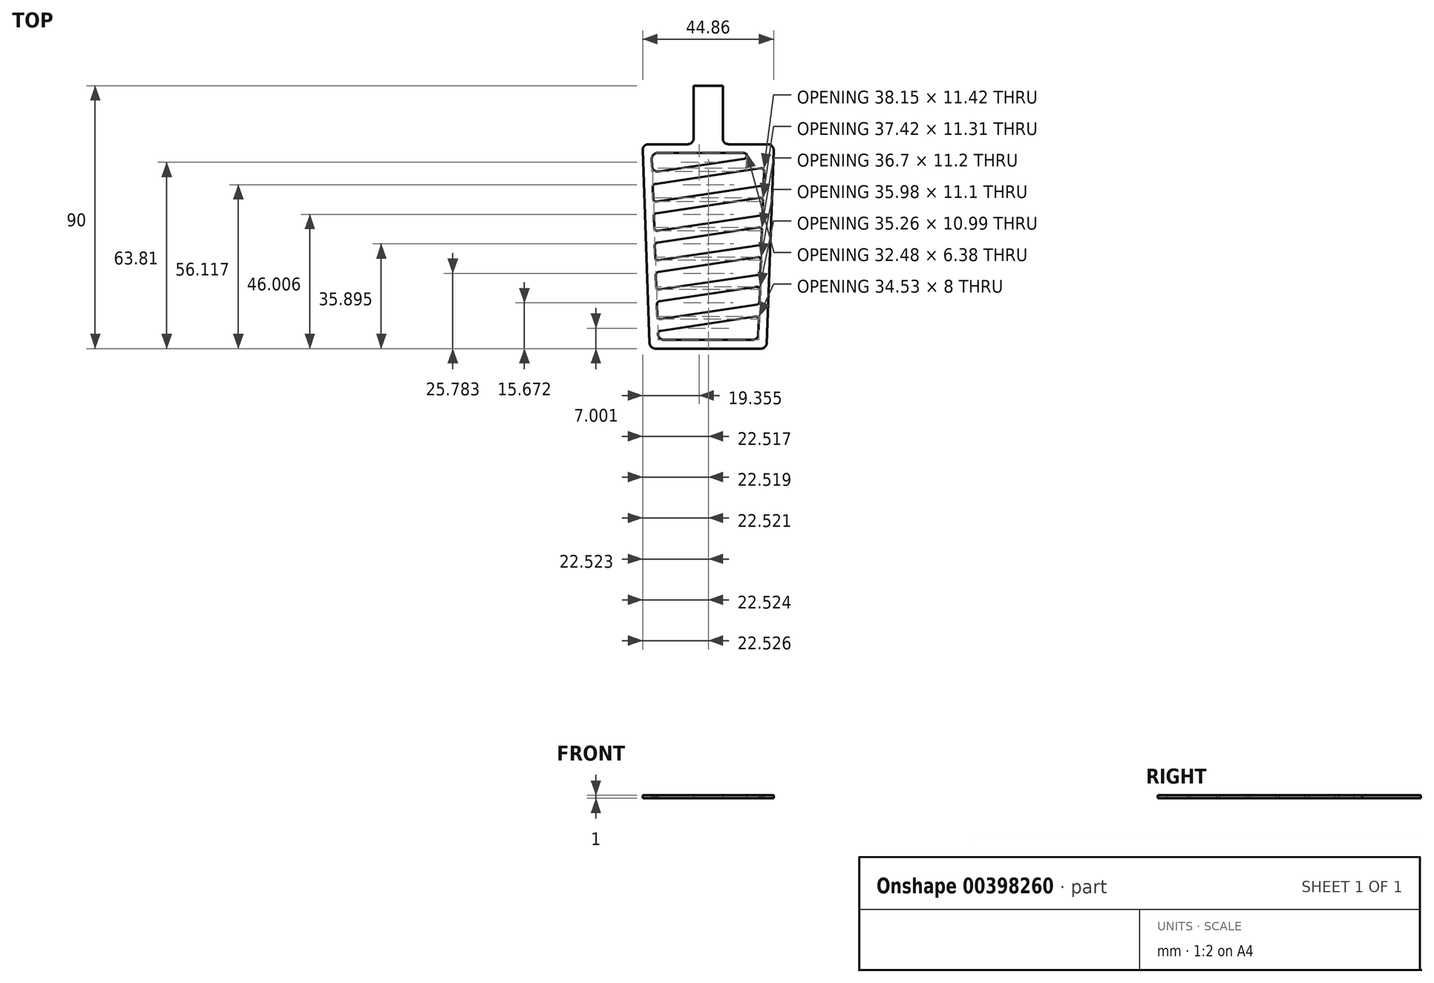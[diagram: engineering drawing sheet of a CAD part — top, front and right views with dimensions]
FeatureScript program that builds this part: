
annotation { "Feature Type Name" : "Feature", "Feature Type Description" : "" }
export const myFeature = defineFeature(function(context is Context, id is Id, definition is map)
    precondition{}
    {
        {
            var Q0;
            Q0=qCreatedBy(makeId("Top.planeOp"),FACE);
            var sketch = newSketch(context, id + "F0", { "sketchPlane" : qUnion([Q0])});
            skLineSegment(sketch, "E0", {"start": v(-20.07, -33.07) * mm, "end": v(-22.43, 32.93) * mm});
            skLineSegment(sketch, "E1", {"start": v(20.07, -33.07) * mm, "end": v(22.43, 32.93) * mm});
            skLineSegment(sketch, "E2", {"start": v(20.43, 35) * mm, "end": v(7, 35) * mm});
            skLineSegment(sketch, "E3", {"start": v(-18.07, -35) * mm, "end": v(18.07, -35) * mm});
            skLineSegment(sketch, "E4", {"start": v(18.02, 26.82) * mm, "end": v(-18.12, 21.42) * mm});
            skLineSegment(sketch, "E5", {"start": v(18.17, 20.78) * mm, "end": v(-17.69, 15.42) * mm});
            skLineSegment(sketch, "E6", {"start": v(17.66, 16.65) * mm, "end": v(-17.77, 11.36) * mm});
            skLineSegment(sketch, "E7", {"start": v(17.8, 10.6) * mm, "end": v(-17.33, 5.36) * mm});
            skLineSegment(sketch, "E8", {"start": v(17.3, 6.49) * mm, "end": v(-17.4, 1.3) * mm});
            skLineSegment(sketch, "E9", {"start": v(17.45, 0.44) * mm, "end": v(-16.97, -4.7) * mm});
            skLineSegment(sketch, "E10", {"start": v(16.93, -3.68) * mm, "end": v(-17.05, -8.76) * mm});
            skLineSegment(sketch, "E11", {"start": v(17.08, -9.72) * mm, "end": v(-16.6, -14.76) * mm});
            skLineSegment(sketch, "E12", {"start": v(16.57, -13.84) * mm, "end": v(-16.69, -18.81) * mm});
            skLineSegment(sketch, "E13", {"start": v(16.72, -19.89) * mm, "end": v(-16.25, -24.81) * mm});
            skLineSegment(sketch, "E14", {"start": v(16.2, -24) * mm, "end": v(-16.33, -28.87) * mm});
            skLineSegment(sketch, "E15.0", {"start": v(17.17, -30.07) * mm, "end": v(17.35, -25.03) * mm});
            skLineSegment(sketch, "E16.0", {"start": v(-17.17, -30.07) * mm, "end": v(-17.18, -29.9) * mm});
            skLineSegment(sketch, "E17.0", {"start": v(-15.18, -32) * mm, "end": v(15.18, -32) * mm});
            skLineSegment(sketch, "E18.0", {"start": v(25, 32) * mm, "end": v(22.4, 32) * mm});
            skLineSegment(sketch, "E19.trimOffspring", {"start": v(12.32, 30.01) * mm, "end": v(-16.94, 25.64) * mm});
            skLineSegment(sketch, "E20.trimOffspring", {"start": v(-22.4, 32) * mm, "end": v(-25, 32) * mm});
            skLineSegment(sketch, "E21.trimOffspring", {"start": v(-18.83, 16.37) * mm, "end": v(-18.98, 20.4) * mm});
            skLineSegment(sketch, "E22.trimOffspring", {"start": v(19.02, 21.73) * mm, "end": v(19.17, 25.8) * mm});
            skLineSegment(sketch, "E23.trimOffspring", {"start": v(18.66, 11.56) * mm, "end": v(18.8, 15.63) * mm});
            skLineSegment(sketch, "E24.trimOffspring", {"start": v(-18.47, 6.31) * mm, "end": v(-18.62, 10.33) * mm});
            skLineSegment(sketch, "E25.trimOffspring", {"start": v(18.3, 1.4) * mm, "end": v(18.44, 5.46) * mm});
            skLineSegment(sketch, "E26.trimOffspring", {"start": v(17.93, -8.77) * mm, "end": v(18.08, -4.7) * mm});
            skLineSegment(sketch, "E27.trimOffspring", {"start": v(-17.76, -13.8) * mm, "end": v(-17.9, -9.78) * mm});
            skLineSegment(sketch, "E28.trimOffspring", {"start": v(17.57, -18.93) * mm, "end": v(17.72, -14.87) * mm});
            skLineSegment(sketch, "E29.trimOffspring", {"start": v(-17.4, -23.86) * mm, "end": v(-17.54, -19.84) * mm});
            skLineSegment(sketch, "E30", {"start": v(-18.11, -3.75) * mm, "end": v(-18.26, 0.28) * mm});
            skLineSegment(sketch, "E31", {"start": v(19.4, 32) * mm, "end": v(19.39, 31.95) * mm});
            skLineSegment(sketch, "E32", {"start": v(12.17, 32) * mm, "end": v(-17.32, 32) * mm});
            skLineSegment(sketch, "E33", {"start": v(-19.23, 27.55) * mm, "end": v(-19.32, 29.93) * mm});
            skLineSegment(sketch, "E34.trimOffspring", {"start": v(19.39, 31.95) * mm, "end": v(19.4, 32) * mm});
            skPoint(sketch, "E35.visualSharp", {"position": v(-22.5, 35) * mm});
            skArc(sketch, "E35.filletArc", {"start": v(-20.43, 35) * mm, "mid": v(-21.87, 34.39) * mm, "end": v(-22.43, 32.93) * mm});
            skPoint(sketch, "E36.visualSharp", {"position": v(-20, -35) * mm});
            skArc(sketch, "E36.filletArc", {"start": v(-20.07, -33.07) * mm, "mid": v(-19.46, -34.44) * mm, "end": v(-18.07, -35) * mm});
            skPoint(sketch, "E37.visualSharp", {"position": v(20, -35) * mm});
            skArc(sketch, "E37.filletArc", {"start": v(18.07, -35) * mm, "mid": v(19.46, -34.44) * mm, "end": v(20.07, -33.07) * mm});
            skPoint(sketch, "E38.visualSharp", {"position": v(22.5, 35) * mm});
            skArc(sketch, "E38.filletArc", {"start": v(22.43, 32.93) * mm, "mid": v(21.87, 34.39) * mm, "end": v(20.43, 35) * mm});
            skPoint(sketch, "E39.visualSharp", {"position": v(-19, 21.28) * mm});
            skArc(sketch, "E39.filletArc", {"start": v(-18.12, 21.42) * mm, "mid": v(-18.75, 21.07) * mm, "end": v(-18.98, 20.4) * mm});
            skPoint(sketch, "E40.visualSharp", {"position": v(-18.8, 15.25) * mm});
            skArc(sketch, "E40.filletArc", {"start": v(-18.83, 16.37) * mm, "mid": v(-18.47, 15.64) * mm, "end": v(-17.69, 15.42) * mm});
            skPoint(sketch, "E41.visualSharp", {"position": v(19, 20.9) * mm});
            skArc(sketch, "E41.filletArc", {"start": v(18.17, 20.78) * mm, "mid": v(18.77, 21.1) * mm, "end": v(19.02, 21.73) * mm});
            skPoint(sketch, "E42.visualSharp", {"position": v(19.21, 27) * mm});
            skArc(sketch, "E42.filletArc", {"start": v(19.17, 25.8) * mm, "mid": v(18.84, 26.58) * mm, "end": v(18.02, 26.82) * mm});
            skPoint(sketch, "E43.visualSharp", {"position": v(18.63, 10.73) * mm});
            skArc(sketch, "E43.filletArc", {"start": v(17.8, 10.6) * mm, "mid": v(18.4, 10.93) * mm, "end": v(18.66, 11.56) * mm});
            skPoint(sketch, "E44.visualSharp", {"position": v(-18.65, 11.23) * mm});
            skArc(sketch, "E44.filletArc", {"start": v(-17.77, 11.36) * mm, "mid": v(-18.39, 11) * mm, "end": v(-18.62, 10.33) * mm});
            skPoint(sketch, "E45.visualSharp", {"position": v(18.85, 16.83) * mm});
            skArc(sketch, "E45.filletArc", {"start": v(18.8, 15.63) * mm, "mid": v(18.47, 16.41) * mm, "end": v(17.66, 16.65) * mm});
            skPoint(sketch, "E46.visualSharp", {"position": v(-18.43, 5.2) * mm});
            skArc(sketch, "E46.filletArc", {"start": v(-18.47, 6.31) * mm, "mid": v(-18.11, 5.58) * mm, "end": v(-17.33, 5.36) * mm});
            skPoint(sketch, "E47.visualSharp", {"position": v(-18.07, -4.86) * mm});
            skArc(sketch, "E47.filletArc", {"start": v(-18.11, -3.75) * mm, "mid": v(-17.75, -4.48) * mm, "end": v(-16.97, -4.7) * mm});
            skPoint(sketch, "E48.visualSharp", {"position": v(-18.29, 1.17) * mm});
            skArc(sketch, "E48.filletArc", {"start": v(-17.4, 1.3) * mm, "mid": v(-18.03, 0.95) * mm, "end": v(-18.26, 0.28) * mm});
            skPoint(sketch, "E49.visualSharp", {"position": v(18.49, 6.67) * mm});
            skArc(sketch, "E49.filletArc", {"start": v(18.44, 5.46) * mm, "mid": v(18.11, 6.25) * mm, "end": v(17.3, 6.49) * mm});
            skPoint(sketch, "E50.visualSharp", {"position": v(18.27, 0.57) * mm});
            skArc(sketch, "E50.filletArc", {"start": v(17.45, 0.44) * mm, "mid": v(18.04, 0.77) * mm, "end": v(18.3, 1.4) * mm});
            skPoint(sketch, "E51.visualSharp", {"position": v(18.12, -3.5) * mm});
            skArc(sketch, "E51.filletArc", {"start": v(18.08, -4.7) * mm, "mid": v(17.75, -3.92) * mm, "end": v(16.93, -3.68) * mm});
            skPoint(sketch, "E52.visualSharp", {"position": v(17.9, -9.6) * mm});
            skArc(sketch, "E52.filletArc", {"start": v(17.08, -9.72) * mm, "mid": v(17.68, -9.4) * mm, "end": v(17.93, -8.77) * mm});
            skPoint(sketch, "E53.visualSharp", {"position": v(-17.72, -14.92) * mm});
            skArc(sketch, "E53.filletArc", {"start": v(-17.76, -13.8) * mm, "mid": v(-17.4, -14.54) * mm, "end": v(-16.6, -14.76) * mm});
            skPoint(sketch, "E54.visualSharp", {"position": v(-17.93, -8.89) * mm});
            skArc(sketch, "E54.filletArc", {"start": v(-17.05, -8.76) * mm, "mid": v(-17.67, -9.1) * mm, "end": v(-17.9, -9.78) * mm});
            skPoint(sketch, "E55.visualSharp", {"position": v(17.76, -13.66) * mm});
            skArc(sketch, "E55.filletArc", {"start": v(17.72, -14.87) * mm, "mid": v(17.38, -14.09) * mm, "end": v(16.57, -13.84) * mm});
            skPoint(sketch, "E56.visualSharp", {"position": v(17.54, -19.76) * mm});
            skArc(sketch, "E56.filletArc", {"start": v(16.72, -19.89) * mm, "mid": v(17.32, -19.56) * mm, "end": v(17.57, -18.93) * mm});
            skPoint(sketch, "E57.visualSharp", {"position": v(-17.36, -24.98) * mm});
            skArc(sketch, "E57.filletArc", {"start": v(-17.4, -23.86) * mm, "mid": v(-17.04, -24.6) * mm, "end": v(-16.25, -24.81) * mm});
            skPoint(sketch, "E58.visualSharp", {"position": v(-17.57, -18.94) * mm});
            skArc(sketch, "E58.filletArc", {"start": v(-16.69, -18.81) * mm, "mid": v(-17.3, -19.16) * mm, "end": v(-17.54, -19.84) * mm});
            skPoint(sketch, "E59.visualSharp", {"position": v(17.4, -23.83) * mm});
            skArc(sketch, "E59.filletArc", {"start": v(17.35, -25.03) * mm, "mid": v(17.02, -24.25) * mm, "end": v(16.2, -24) * mm});
            skPoint(sketch, "E60.visualSharp", {"position": v(-17.21, -29) * mm});
            skArc(sketch, "E60.filletArc", {"start": v(-16.33, -28.87) * mm, "mid": v(-16.95, -29.22) * mm, "end": v(-17.18, -29.9) * mm});
            skArc(sketch, "E61.filletArc", {"start": v(12.32, 30.01) * mm, "mid": v(13.17, 31.07) * mm, "end": v(12.17, 32) * mm});
            skPoint(sketch, "E62.visualSharp", {"position": v(-19.4, 32) * mm});
            skArc(sketch, "E62.filletArc", {"start": v(-17.32, 32) * mm, "mid": v(-18.76, 31.39) * mm, "end": v(-19.32, 29.93) * mm});
            skPoint(sketch, "E63.visualSharp", {"position": v(-19.15, 25.3) * mm});
            skArc(sketch, "E63.filletArc", {"start": v(-19.23, 27.55) * mm, "mid": v(-18.51, 26.08) * mm, "end": v(-16.94, 25.64) * mm});
            skPoint(sketch, "E64.visualSharp", {"position": v(17.1, -32) * mm});
            skArc(sketch, "E64.filletArc", {"start": v(15.18, -32) * mm, "mid": v(16.56, -31.44) * mm, "end": v(17.17, -30.07) * mm});
            skPoint(sketch, "E65.visualSharp", {"position": v(-17.1, -32) * mm});
            skArc(sketch, "E65.filletArc", {"start": v(-17.17, -30.07) * mm, "mid": v(-16.56, -31.44) * mm, "end": v(-15.18, -32) * mm});
            skLineSegment(sketch, "E66", {"start": v(-5, 37) * mm, "end": v(-5, 55) * mm});
            skLineSegment(sketch, "E67", {"start": v(-5, 55) * mm, "end": v(5, 55) * mm});
            skLineSegment(sketch, "E68", {"start": v(5, 55) * mm, "end": v(5, 37) * mm});
            skArc(sketch, "E69.filletArc", {"start": v(5, 37) * mm, "mid": v(5.59, 35.59) * mm, "end": v(7, 35) * mm});
            skLineSegment(sketch, "E70", {"start": v(-20.43, 35) * mm, "end": v(-7, 35) * mm});
            skPoint(sketch, "E71.visualSharp", {"position": v(-5, 35) * mm});
            skArc(sketch, "E71.filletArc", {"start": v(-7, 35) * mm, "mid": v(-5.59, 35.59) * mm, "end": v(-5, 37) * mm});
            skSolve(sketch);
        }
        {
            var Q0;
            Q0=makeQuery(id+"F0.imprint","IMPRINT",FACE,{"disambiguationData":[TD([[makeQuery(id+"F0.imprint","IMPRINT",EDGE,{"derivedFrom":sQuery(id+"F0.wireOp",EDGE,"E3")}),1.0]])]});
            var Q1;
            {var subQ0=sQuery(id+"F0.wireOp",EDGE,"E66");Q1=makeQuery(id+"F0.imprint","IMPRINT",FACE,{"disambiguationData":[TD([[makeQuery(id+"F0.imprint","IMPRINT",EDGE,{"derivedFrom":subQ0}),-1.0]])]});}
            extrude(context, id + "F1", {"entities" : qUnion([Q0, Q1]), "depth" : 1 * mm});
        }
    });
